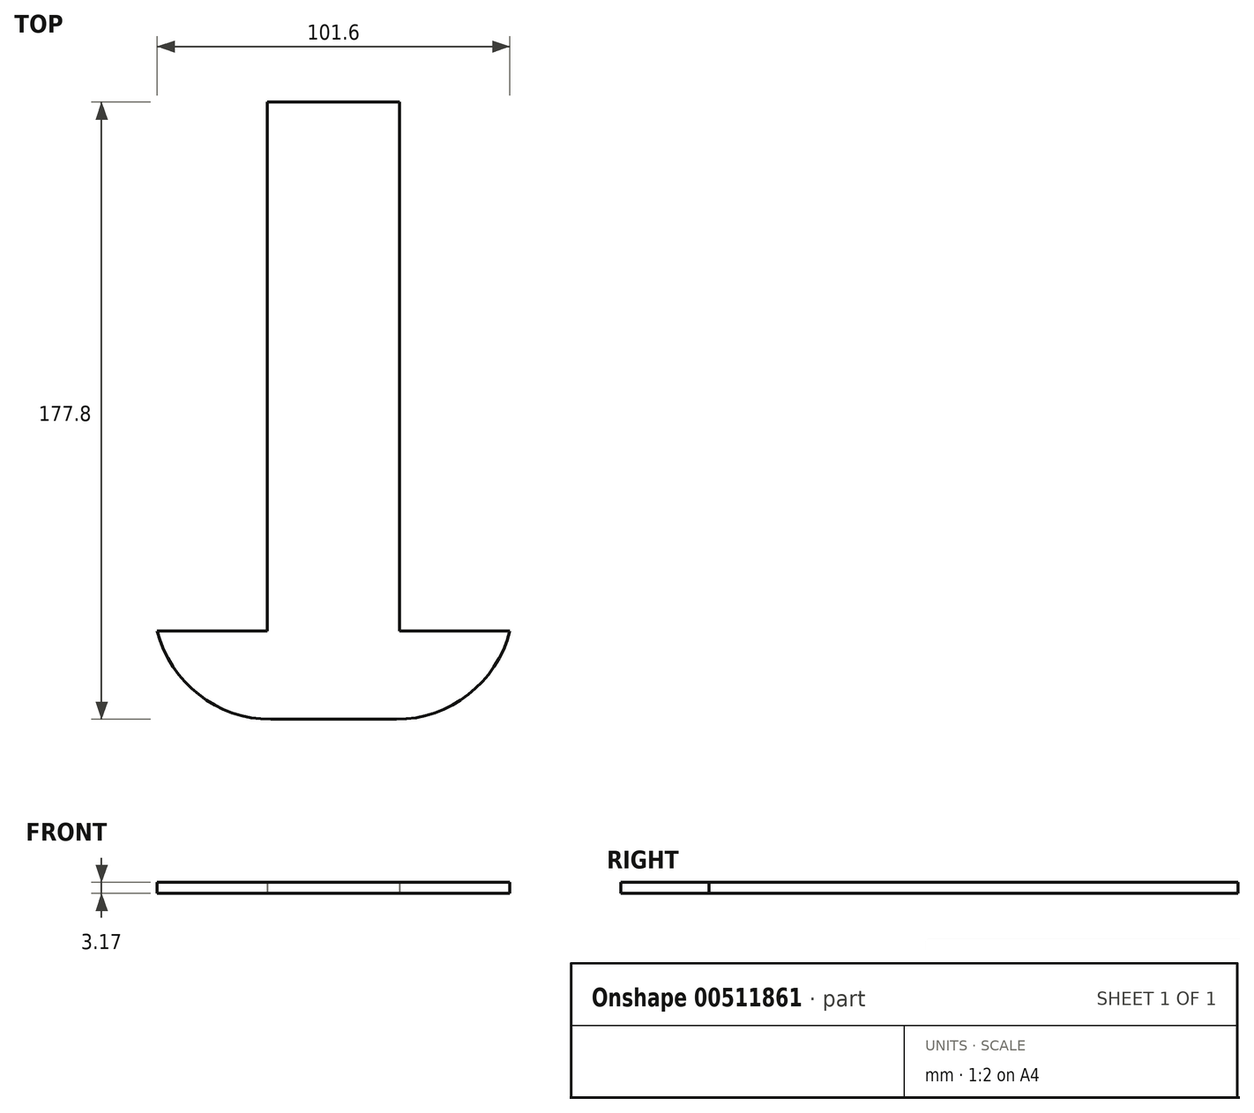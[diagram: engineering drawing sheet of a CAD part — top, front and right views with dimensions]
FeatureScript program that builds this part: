
annotation { "Feature Type Name" : "Feature", "Feature Type Description" : "" }
export const myFeature = defineFeature(function(context is Context, id is Id, definition is map)
    precondition{}
    {
        {
            var Q0;
            Q0=qCreatedBy(makeId("Top.planeOp"),FACE);
            var sketch = newSketch(context, id + "F0", { "sketchPlane" : qUnion([Q0])});
            skLineSegment(sketch, "E0.bottom", {"start": v(19.05, 76.2) * mm, "end": v(-19.05, 76.2) * mm});
            skLineSegment(sketch, "E0.left", {"start": v(19.05, 76.2) * mm, "end": v(19.05, -76.2) * mm});
            skLineSegment(sketch, "E0.right", {"start": v(-19.05, 76.2) * mm, "end": v(-19.05, -76.2) * mm});
            skPoint(sketch, "E0.middle", {"position": v(0, 0) * mm});
            skLineSegment(sketch, "E1.bottom", {"start": v(50.8, -76.2) * mm, "end": v(19.05, -76.2) * mm});
            skLineSegment(sketch, "E1.top", {"start": v(50.8, -101.6) * mm, "end": v(-50.8, -101.6) * mm});
            skLineSegment(sketch, "E1.left", {"start": v(50.8, -76.2) * mm, "end": v(50.8, -101.6) * mm});
            skLineSegment(sketch, "E1.right", {"start": v(-50.8, -76.2) * mm, "end": v(-50.8, -101.6) * mm});
            skPoint(sketch, "E1.middle", {"position": v(0, -88.9) * mm});
            skPoint(sketch, "E1.middle.positionSnap0", {"position": v(0, -76.2) * mm});
            skPoint(sketch, "E1.cornerSnap0", {"position": v(0, -76.2) * mm});
            skPoint(sketch, "E1.centerSnap0", {"position": v(0, -76.2) * mm});
            skLineSegment(sketch, "E2.trimOffspring", {"start": v(-19.05, -76.2) * mm, "end": v(-50.8, -76.2) * mm});
            skSolve(sketch);
        }
        {
            var Q0;
            Q0=makeQuery(id+"F0.imprint","IMPRINT",FACE,{"disambiguationData":[TD([[makeQuery(id+"F0.imprint","IMPRINT",EDGE,{"derivedFrom":sQuery(id+"F0.wireOp",EDGE,"E0.bottom")}),1.0]])]});
            extrude(context, id + "F1", {"entities" : qUnion([Q0]), "depth" : 3.17 * mm, "offsetDistance" : 25.4 * mm});
        }
        {
            var Q0;
            Q0=makeQuery(id+"F1.opExtrude","SWEPT_EDGE",EDGE,{"disambiguationData":[OSD([sQuery(id+"F0.wireOp",EDGE,"E1.top"),sQuery(id+"F0.wireOp",EDGE,"E1.right")])]});
            var Q1;
            Q1=makeQuery(id+"F1.opExtrude","SWEPT_EDGE",EDGE,{"disambiguationData":[OSD([sQuery(id+"F0.wireOp",EDGE,"E1.top"),sQuery(id+"F0.wireOp",EDGE,"E1.left")])]});
            fillet(context, id + "F2", {"entities" : qUnion([Q0, Q1]), "radius" : 33.73 * mm, "tangentPropagation" : true, "allowEdgeOverflow" : false});
        }
    });
